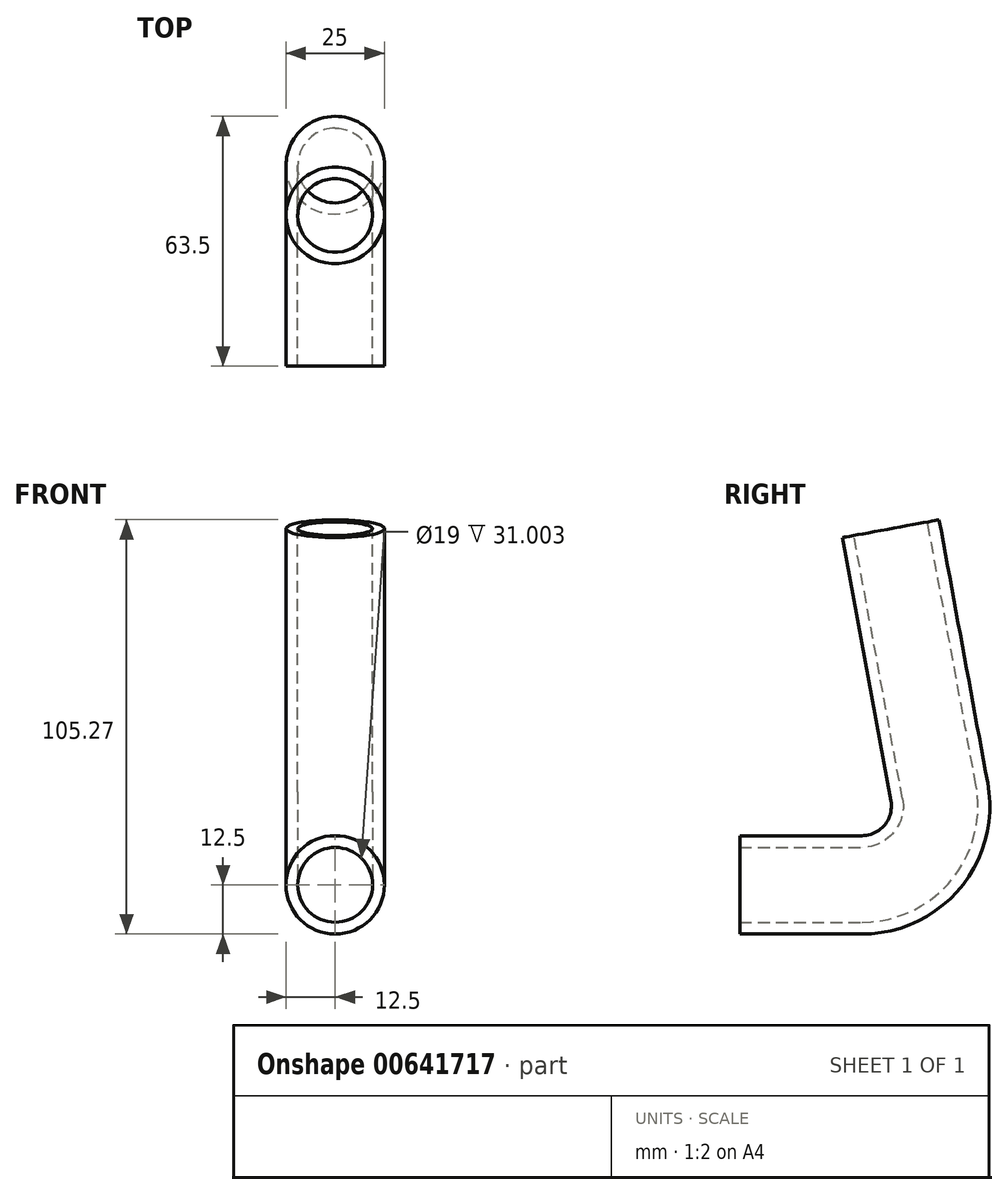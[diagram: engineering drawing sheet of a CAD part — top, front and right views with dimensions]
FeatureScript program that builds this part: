
annotation { "Feature Type Name" : "Feature", "Feature Type Description" : "" }
export const myFeature = defineFeature(function(context is Context, id is Id, definition is map)
    precondition{}
    {
        {
            var Q0;
            Q0=qCreatedBy(makeId("Front.planeOp"),FACE);
            var sketch = newSketch(context, id + "F0", { "sketchPlane" : qUnion([Q0])});
            skCircle(sketch, "E0", {"center": v(0, 0) * mm, "radius": 9.5 * mm});
            skCircle(sketch, "E1.0", {"center": v(0, 0) * mm, "radius": 12.5 * mm});
            skSolve(sketch);
        }
        {
            var Q0;
            Q0=qCreatedBy(makeId("Right.planeOp"),FACE);
            var sketch = newSketch(context, id + "F1", { "sketchPlane" : qUnion([Q0])});
            skLineSegment(sketch, "E2", {"start": v(0, 0) * mm, "end": v(31, 0) * mm});
            skLineSegment(sketch, "E3", {"start": v(50.67, 23.63) * mm, "end": v(38.33, 90.5) * mm});
            skPoint(sketch, "E4.visualSharp", {"position": v(55.03, 0) * mm});
            skArc(sketch, "E4.filletArc", {"start": v(31, 0) * mm, "mid": v(46.38, 7.2) * mm, "end": v(50.67, 23.63) * mm});
            skSolve(sketch);
        }
        {
            var Q0;
            Q0=makeQuery(id+"F0.imprint","IMPRINT",FACE,{"disambiguationData":[TD([[makeQuery(id+"F0.imprint","IMPRINT",EDGE,{"derivedFrom":sQuery(id+"F0.wireOp",EDGE,"E0")}),-1.0]])]});
            var Q1;
            Q1=sQuery(id+"F1.wireOp",EDGE,"E2");
            var Q2;
            Q2=sQuery(id+"F1.wireOp",EDGE,"E4.filletArc");
            var Q3;
            Q3=sQuery(id+"F1.wireOp",EDGE,"E3");
            sweep(context, id + "F2", {"profiles" : qUnion([Q0]), "path" : qUnion([Q1, Q2, Q3])});
        }
    });
